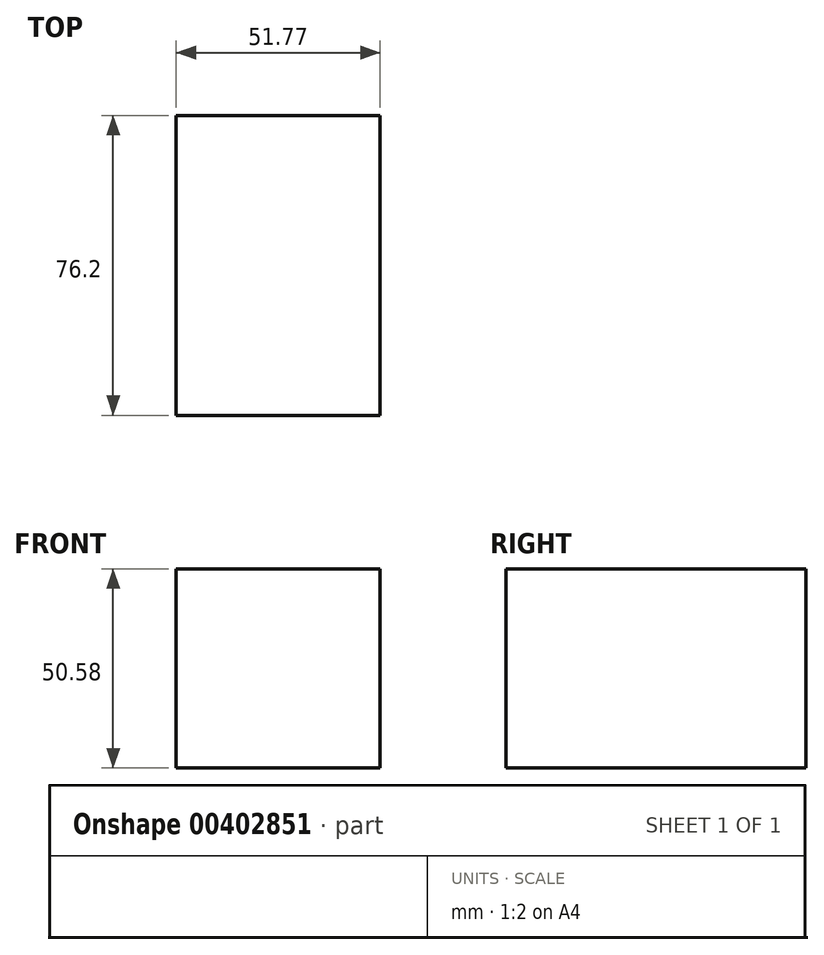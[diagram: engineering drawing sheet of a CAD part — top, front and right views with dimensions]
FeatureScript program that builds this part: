
annotation { "Feature Type Name" : "Feature", "Feature Type Description" : "" }
export const myFeature = defineFeature(function(context is Context, id is Id, definition is map)
    precondition{}
    {
        {
            var Q0;
            Q0=qCreatedBy(makeId("Front.planeOp"),FACE);
            var sketch = newSketch(context, id + "F0", { "sketchPlane" : qUnion([Q0])});
            skLineSegment(sketch, "E0.bottom", {"start": v(-24.82, 41.72) * mm, "end": v(26.95, 41.72) * mm});
            skLineSegment(sketch, "E0.top", {"start": v(-24.82, -8.86) * mm, "end": v(26.95, -8.86) * mm});
            skLineSegment(sketch, "E0.left", {"start": v(-24.82, 41.72) * mm, "end": v(-24.82, -8.86) * mm});
            skLineSegment(sketch, "E0.right", {"start": v(26.95, 41.72) * mm, "end": v(26.95, -8.86) * mm});
            skSolve(sketch);
        }
        {
            var Q0;
            Q0 = qSketchRegion(id + "F0", true);
            extrude(context, id + "F1", {"entities" : qUnion([Q0]), "depth" : 25.4 * mm});
        }
        {
            var Q0;
            Q0=makeQuery(id+"F1.opExtrude","CAP_FACE",FACE,{"disambiguationData":[OSD([sQuery(id+"F0.wireOp",EDGE,"E0.bottom"),sQuery(id+"F0.wireOp",EDGE,"E0.top"),sQuery(id+"F0.wireOp",EDGE,"E0.left"),sQuery(id+"F0.wireOp",EDGE,"E0.right")])],"isStart":false});
            var sketch = newSketch(context, id + "F2", { "sketchPlane" : qUnion([Q0])});
            skSolve(sketch);
        }
        {
            var Q0;
            Q0 = qSketchRegion(id + "F2", true);
            var Q1;
            Q1=makeQuery(id+"F2.imprint","IMPRINT",FACE,{"disambiguationData":[TD([[makeQuery(id+"F2.imprint","IMPRINT",EDGE,{"derivedFrom":makeQuery(id+"F1.opExtrude","CAP_EDGE",EDGE,{"disambiguationData":[OSD([sQuery(id+"F0.wireOp",EDGE,"E0.bottom")])],"isStart":false})}),-1.0]])]});
            extrude(context, id + "F3", {"entities" : qUnion([Q0, Q1]), "operationType" : NewBodyOperationType.ADD, "depth" : 50.8 * mm});
        }
    });
